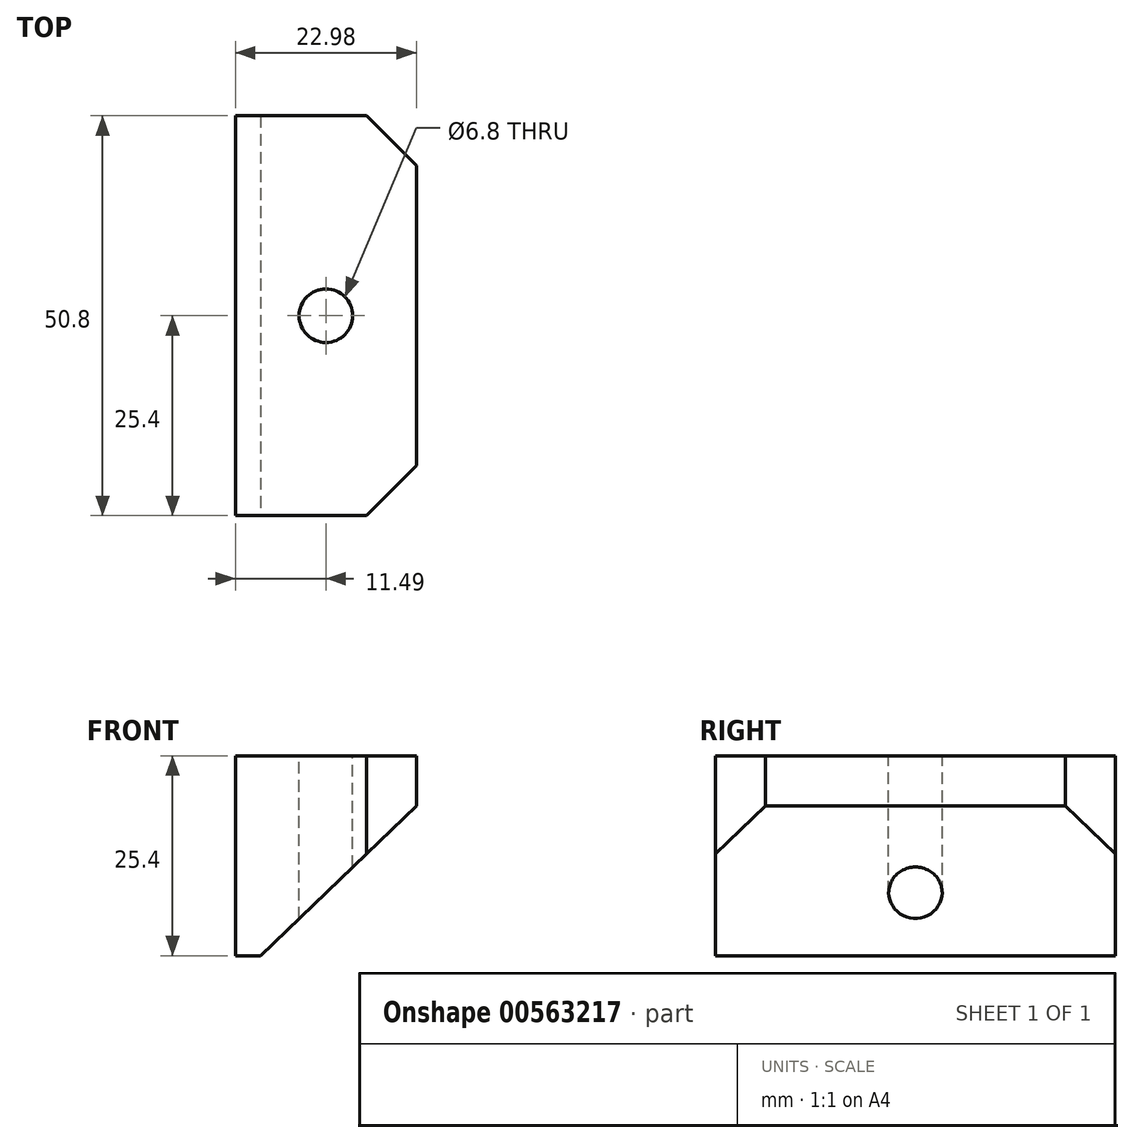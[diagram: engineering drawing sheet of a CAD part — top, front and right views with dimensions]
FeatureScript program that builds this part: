
annotation { "Feature Type Name" : "Feature", "Feature Type Description" : "" }
export const myFeature = defineFeature(function(context is Context, id is Id, definition is map)
    precondition{}
    {
        {
            var Q0;
            Q0=qCreatedBy(makeId("Front.planeOp"),FACE);
            var sketch = newSketch(context, id + "F0", { "sketchPlane" : qUnion([Q0])});
            skLineSegment(sketch, "E0.bottom", {"start": v(-11.5, 12.7) * mm, "end": v(11.5, 12.7) * mm});
            skLineSegment(sketch, "E0.top", {"start": v(-11.5, -12.7) * mm, "end": v(11.5, -12.7) * mm});
            skLineSegment(sketch, "E0.left", {"start": v(-11.5, 12.7) * mm, "end": v(-11.5, -12.7) * mm});
            skLineSegment(sketch, "E0.right", {"start": v(11.5, 12.7) * mm, "end": v(11.5, -12.7) * mm});
            skPoint(sketch, "E0.middle", {"position": v(0, 0) * mm});
            skSolve(sketch);
        }
        {
            var Q0;
            Q0=makeQuery(id+"F0.imprint","IMPRINT",FACE,{"disambiguationData":[TD([[makeQuery(id+"F0.imprint","IMPRINT",EDGE,{"derivedFrom":sQuery(id+"F0.wireOp",EDGE,"E0.bottom")}),-1.0]])]});
            extrude(context, id + "F1", {"entities" : qUnion([Q0]), "endBound" : BoundingType.SYMMETRIC, "depth" : 50.8 * mm, "offsetDistance" : 25.4 * mm});
        }
        {
            var Q0;
            Q0=makeQuery(id+"F1.opExtrude","SWEPT_FACE",FACE,{"disambiguationData":[OSD([sQuery(id+"F0.wireOp",EDGE,"E0.bottom")])]});
            var sketch = newSketch(context, id + "F2", { "sketchPlane" : qUnion([Q0])});
            skPoint(sketch, "E1", {"position": v(0, 0) * mm});
            skSolve(sketch);
        }
        {
            var Q0;
            Q0=sQuery(id+"F2.wireOp",VERTEX,"E1");
            var Q1;
            Q1=makeQuery(id+"F1.opExtrude","SWEPT_BODY",BODY,{"disambiguationData":[OSD([sQuery(id+"F0.wireOp",EDGE,"E0.bottom"),sQuery(id+"F0.wireOp",EDGE,"E0.top"),sQuery(id+"F0.wireOp",EDGE,"E0.left"),sQuery(id+"F0.wireOp",EDGE,"E0.right")])]});
            hole(context, id + "F3", {"style" : HoleStyle.SIMPLE, "endStyle" : HoleEndStyle.THROUGH, "standardTappedOrClearance" : lookupTablePath({ "standard" : "ISO", "engagement" : "75%", "pitch" : "1.25 mm", "size" : "M8", "type" : "Tapped" }), "standardBlindInLast" : lookupTablePath({ "standard" : "ISO", "engagement" : "75%", "pitch" : "1.25 mm", "size" : "M8", "type" : "Tapped" }), "holeDiameter" : 6.8 * mm, "showTappedDepth" : true, "isTappedThrough" : true, "tappedDepth" : 34.3 * mm, "tapClearance" : 3, "locations" : qUnion([Q0]), "scope" : qUnion([Q1]), "majorDiameter" : 8 * mm});
        }
        {
            var Q0;
            Q0=makeQuery(id+"F1.opExtrude","CAP_EDGE",EDGE,{"disambiguationData":[OSD([sQuery(id+"F0.wireOp",EDGE,"E0.right")])],"isStart":false});
            chamfer(context, id + "F4", {"entities" : qUnion([Q0]), "width" : 6.35 * mm, "tangentPropagation" : true});
        }
        {
            var Q0;
            Q0=makeQuery(id+"F1.opExtrude","CAP_EDGE",EDGE,{"disambiguationData":[OSD([sQuery(id+"F0.wireOp",EDGE,"E0.right")])],"isStart":true});
            chamfer(context, id + "F5", {"entities" : qUnion([Q0]), "width" : 6.35 * mm, "tangentPropagation" : true});
        }
        {
            var Q0;
            Q0=makeQuery(id+"F1.opExtrude","SWEPT_EDGE",EDGE,{"disambiguationData":[OSD([sQuery(id+"F0.wireOp",EDGE,"E0.top"),sQuery(id+"F0.wireOp",EDGE,"E0.right")])]});
            chamfer(context, id + "F6", {"entities" : qUnion([Q0]), "chamferType" : ChamferType.TWO_OFFSETS, "width1" : 19.05 * mm, "oppositeDirection" : false, "width2" : 19.8 * mm, "tangentPropagation" : true});
        }
    });
